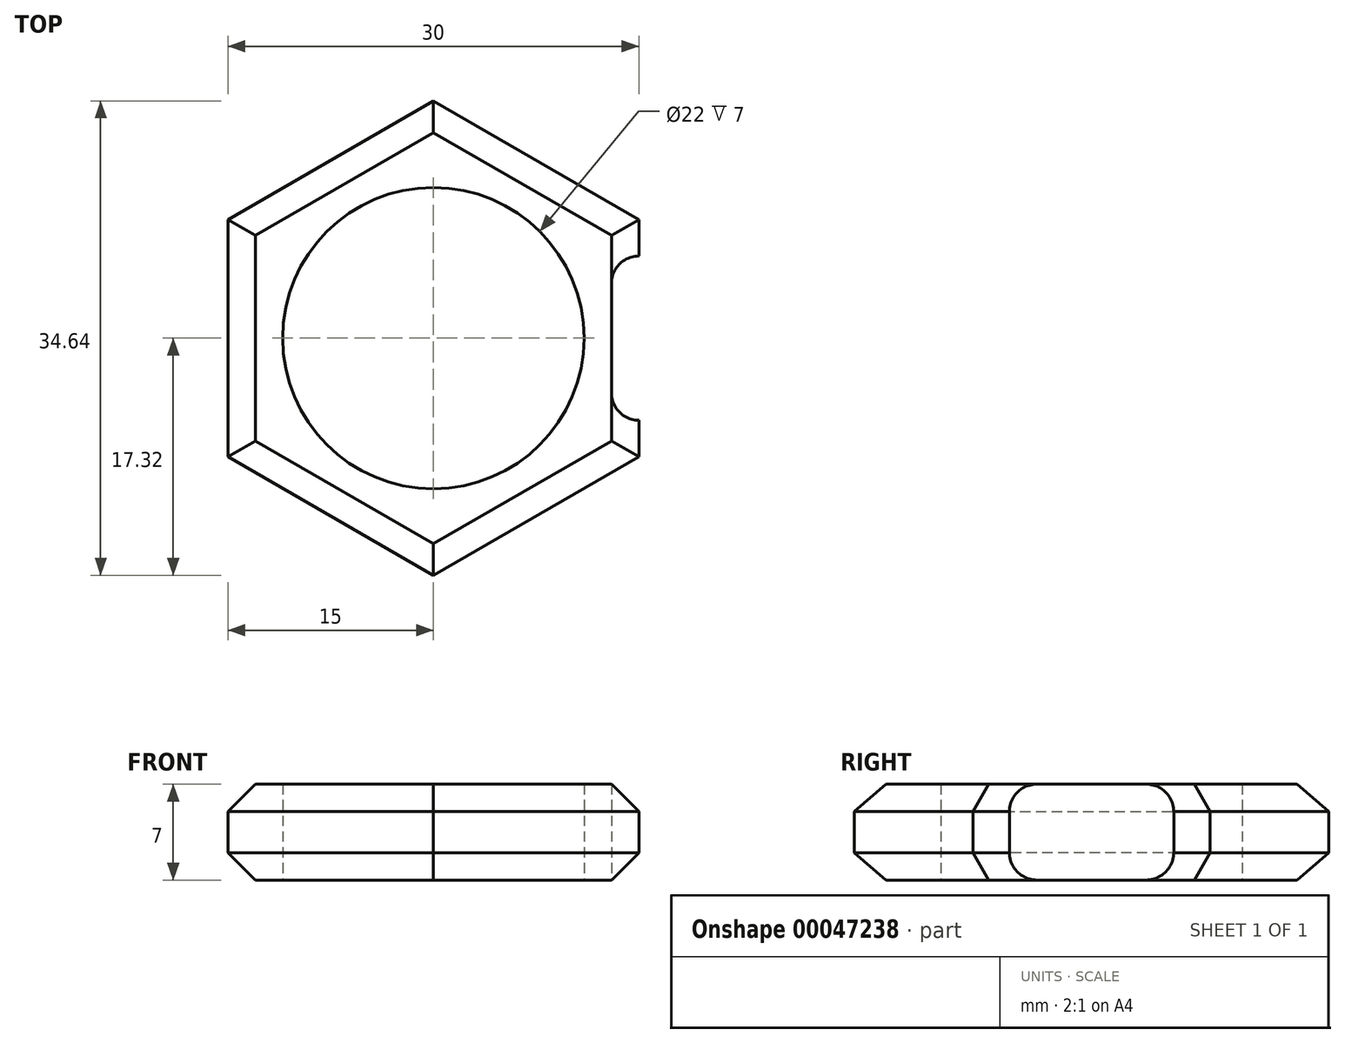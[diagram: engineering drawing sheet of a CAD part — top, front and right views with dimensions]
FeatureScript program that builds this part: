
annotation { "Feature Type Name" : "Feature", "Feature Type Description" : "" }
export const myFeature = defineFeature(function(context is Context, id is Id, definition is map)
    precondition{}
    {
        {
            var Q0;
            Q0=qCreatedBy(makeId("Top.planeOp"),FACE);
            var sketch = newSketch(context, id + "F0", { "sketchPlane" : qUnion([Q0])});
            skCircle(sketch, "E0", {"center": v(0, 0) * mm, "radius": 11 * mm});
            skCircle(sketch, "E1.cCircle", {"center": v(0, 0) * mm, "radius": 15 * mm, "construction": true});
            skPoint(sketch, "E1.0.midPoint", {"position": v(15, 0) * mm});
            skLineSegment(sketch, "E2.0", {"start": v(15, 8.66) * mm, "end": v(15, -8.66) * mm});
            skLineSegment(sketch, "E2.1", {"start": v(15, -8.66) * mm, "end": v(0, -17.32) * mm});
            skLineSegment(sketch, "E2.2", {"start": v(0, -17.32) * mm, "end": v(-15, -8.66) * mm});
            skLineSegment(sketch, "E2.3", {"start": v(-15, -8.66) * mm, "end": v(-15, 8.66) * mm});
            skLineSegment(sketch, "E2.4", {"start": v(-15, 8.66) * mm, "end": v(0, 17.32) * mm});
            skLineSegment(sketch, "E2.5", {"start": v(0, 17.32) * mm, "end": v(15, 8.66) * mm});
            skSolve(sketch);
        }
        {
            var Q0;
            Q0 = qSketchRegion(id + "F0", true);
            extrude(context, id + "F1", {"entities" : qUnion([Q0]), "depth" : 7 * mm});
        }
        {
            var Q0;
            Q0=makeQuery(id+"F1.opExtrude","CAP_EDGE",EDGE,{"disambiguationData":[OSD([sQuery(id+"F0.wireOp",EDGE,"E2.3")])],"isStart":false});
            var Q1;
            Q1=makeQuery(id+"F1.opExtrude","CAP_EDGE",EDGE,{"disambiguationData":[OSD([sQuery(id+"F0.wireOp",EDGE,"E2.4")])],"isStart":false});
            var Q2;
            Q2=makeQuery(id+"F1.opExtrude","CAP_EDGE",EDGE,{"disambiguationData":[OSD([sQuery(id+"F0.wireOp",EDGE,"E2.5")])],"isStart":false});
            var Q3;
            Q3=makeQuery(id+"F1.opExtrude","CAP_EDGE",EDGE,{"disambiguationData":[OSD([sQuery(id+"F0.wireOp",EDGE,"E2.0")])],"isStart":false});
            var Q4;
            Q4=makeQuery(id+"F1.opExtrude","CAP_EDGE",EDGE,{"disambiguationData":[OSD([sQuery(id+"F0.wireOp",EDGE,"E2.1")])],"isStart":false});
            var Q5;
            Q5=makeQuery(id+"F1.opExtrude","CAP_EDGE",EDGE,{"disambiguationData":[OSD([sQuery(id+"F0.wireOp",EDGE,"E2.2")])],"isStart":false});
            var Q6;
            Q6=makeQuery(id+"F1.opExtrude","CAP_EDGE",EDGE,{"disambiguationData":[OSD([sQuery(id+"F0.wireOp",EDGE,"E2.3")])],"isStart":true});
            var Q7;
            Q7=makeQuery(id+"F1.opExtrude","CAP_EDGE",EDGE,{"disambiguationData":[OSD([sQuery(id+"F0.wireOp",EDGE,"E2.4")])],"isStart":true});
            var Q8;
            Q8=makeQuery(id+"F1.opExtrude","CAP_EDGE",EDGE,{"disambiguationData":[OSD([sQuery(id+"F0.wireOp",EDGE,"E2.5")])],"isStart":true});
            var Q9;
            Q9=makeQuery(id+"F1.opExtrude","CAP_EDGE",EDGE,{"disambiguationData":[OSD([sQuery(id+"F0.wireOp",EDGE,"E2.0")])],"isStart":true});
            var Q10;
            Q10=makeQuery(id+"F1.opExtrude","CAP_EDGE",EDGE,{"disambiguationData":[OSD([sQuery(id+"F0.wireOp",EDGE,"E2.1")])],"isStart":true});
            var Q11;
            Q11=makeQuery(id+"F1.opExtrude","CAP_EDGE",EDGE,{"disambiguationData":[OSD([sQuery(id+"F0.wireOp",EDGE,"E2.2")])],"isStart":true});
            chamfer(context, id + "F2", {"entities" : qUnion([Q0, Q1, Q2, Q3, Q4, Q5, Q6, Q7, Q8, Q9, Q10, Q11]), "width" : 2 * mm, "tangentPropagation" : true});
        }
        {
            var Q0;
            Q0=qCreatedBy(makeId("Top.planeOp"),FACE);
            var sketch = newSketch(context, id + "F3", { "sketchPlane" : qUnion([Q0])});
            skLineSegment(sketch, "E3.0", {"start": v(15, 10.9) * mm, "end": v(15, -10.9) * mm});
            skArc(sketch, "E4", {"start": v(15, 6) * mm, "mid": v(13.59, 5.41) * mm, "end": v(13, 4) * mm});
            skArc(sketch, "E5", {"start": v(13, -4) * mm, "mid": v(13.59, -5.41) * mm, "end": v(15, -6) * mm});
            skLineSegment(sketch, "E6", {"start": v(17, -4) * mm, "end": v(17, 4) * mm});
            skLineSegment(sketch, "E7", {"start": v(13, 4) * mm, "end": v(13, -4) * mm});
            skLineSegment(sketch, "E8", {"start": v(15, -6) * mm, "end": v(17, -6) * mm});
            skLineSegment(sketch, "E9", {"start": v(17, -6) * mm, "end": v(17, -4) * mm});
            skLineSegment(sketch, "E10", {"start": v(15, 6) * mm, "end": v(17, 6) * mm});
            skLineSegment(sketch, "E11", {"start": v(17, 6) * mm, "end": v(17, 4) * mm});
            skSolve(sketch);
        }
        {
            var Q0;
            Q0 = qSketchRegion(id + "F3", true);
            extrude(context, id + "F4", {"entities" : qUnion([Q0]), "operationType" : NewBodyOperationType.REMOVE, "depth" : 25 * mm});
        }
    });
